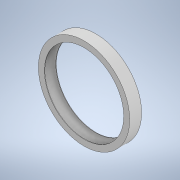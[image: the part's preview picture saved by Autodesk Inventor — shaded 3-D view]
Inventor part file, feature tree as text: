
AUTODESK INVENTOR PART (.ipt)
format: ipt  version: 2022 (Build 260153000, 153)  size: 138,240 bytes
history: native  units: in
note: dims shown in document units (in); Inventor stores cm internally (conversion verified against a paired STEP export)
features: revolve x1, sketch x1
ambient origin geometry x8: Origin, YZ Plane, XZ Plane, XY Plane, X Axis, Y Axis, Z Axis, Center Point
bodies: Body1 (feature_tree)
feature tree (2):
  revolve  "Revolution2"  [1 undecoded]
  sketch  "Sketch1"  dims[d0=0.6in d1=0.3in d3=0.3in d5=0.275in d6=0.5in d7=0.4in d9=2.0in d10=90.0deg d11=0.0344in]
note: 1 required parameter value undecoded (feature->parameter linkage not recoverable at this tier; creation-order binding heuristic only, values carry confidence <= 0.55)
